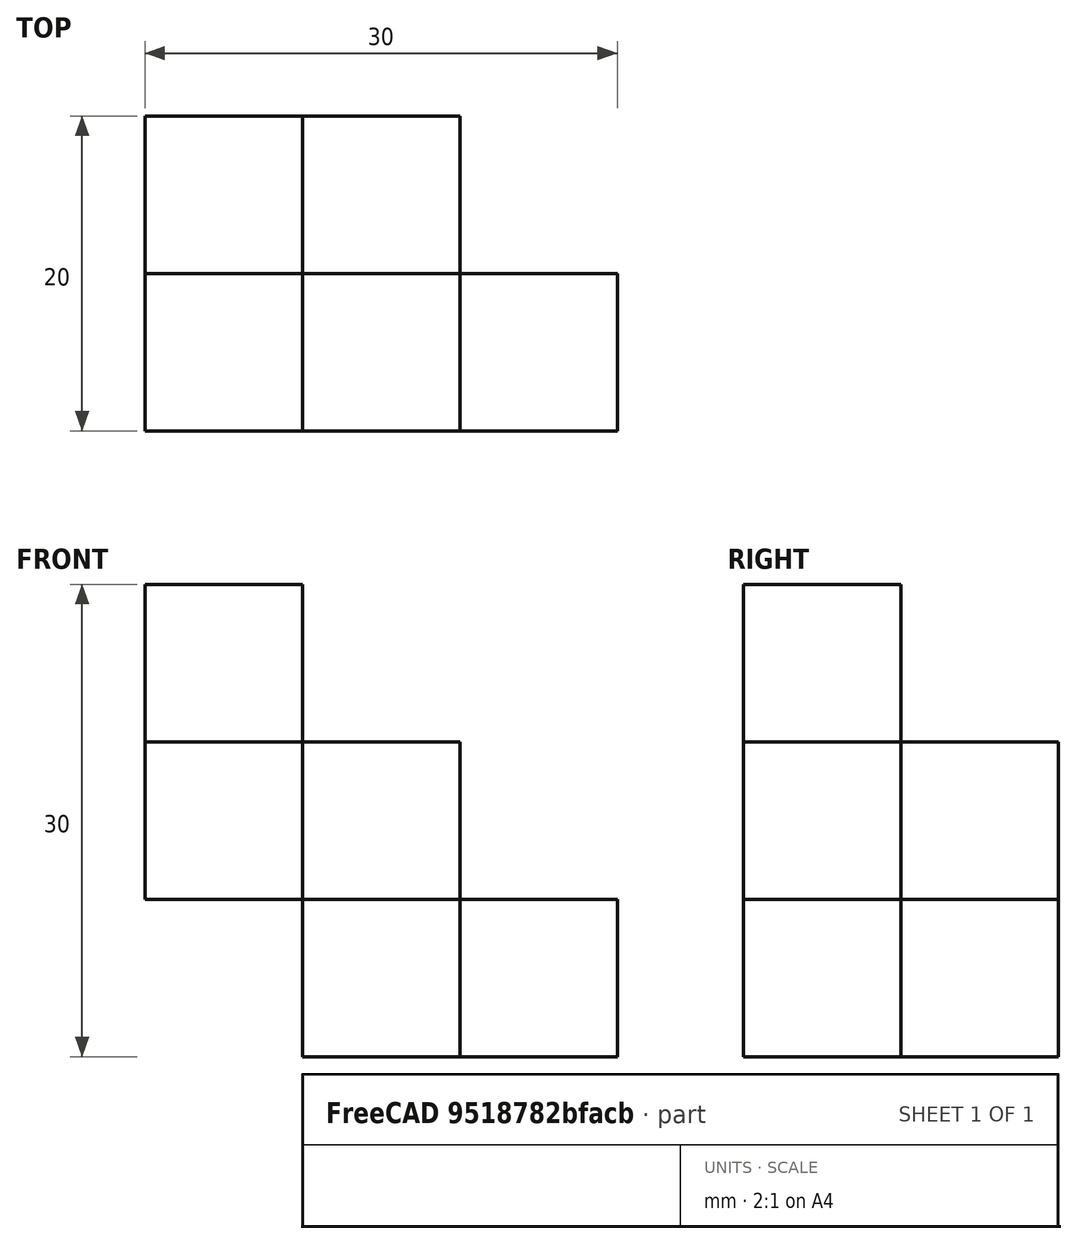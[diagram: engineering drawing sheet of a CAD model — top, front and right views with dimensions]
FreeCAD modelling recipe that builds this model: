
FCSTD DOCUMENT  (FreeCAD 0.21R33694 (Git))
Label: OJT1_T01RO_2_Pràctica3
License: All rights reserved
LicenseURL: https://en.wikipedia.org/wiki/All_rights_reserved
objects: Part::Box×6
note: 6 computed .brp shape members not serialized (recipe doc carries the construction recipe); baked Part::Feature solids carry a one-line shape summary decoded from their .brp

FEATURE [Part::Box] Box  label="Nivel 1"
  AttacherType = Attacher::AttachEngine3D
  Height = 10
  Length = 10
  Placement = pos=(0,0,10) rot=(0,0,1;0rad)
  Width = 10
  expr: .Placement.Base.z = 10
FEATURE [Part::Box] Box001  label=" Nivel 2 - Cubo 2 "
  AttacherType = Attacher::AttachEngine3D
  Height = 10
  Length = 10
  Placement = pos=(0,10,0) rot=(0,0,1;0rad)
  Width = 10
  expr: .Placement.Base.x = 0
FEATURE [Part::Box] Box002  label="Nivel 2- Cubo 1 "
  AttacherType = Attacher::AttachEngine3D
  Height = 10
  Length = 10
  Placement = pos=(10,0,0) rot=(0,0,1;0rad)
  Width = 10
FEATURE [Part::Box] Box003  label="NIvel 3 - Cubo 1"
  AttacherType = Attacher::AttachEngine3D
  Height = 10
  Length = 10
  Placement = pos=(20,0,-10) rot=(0,0,1;0rad)
  Width = 10
  expr: .Placement.Base.z = -10
FEATURE [Part::Box] Box004  label="Nivel 3- Cubo 2"
  AttacherType = Attacher::AttachEngine3D
  Height = 10
  Length = 10
  Placement = pos=(10,10,-10) rot=(0,0,1;0rad)
  Width = 10
  expr: .Placement.Base.x = 10
  expr: .Placement.Base.y = 10
  expr: .Placement.Base.z = -10
FEATURE [Part::Box] Box005  label="Nivel- 3 - cubo 3"
  AttacherType = Attacher::AttachEngine3D
  Height = 10
  Length = 10
  Width = 10
  expr: .Placement.Base.x = 0
  expr: .Placement.Base.y = 20
  expr: .Placement.Base.z = -10
